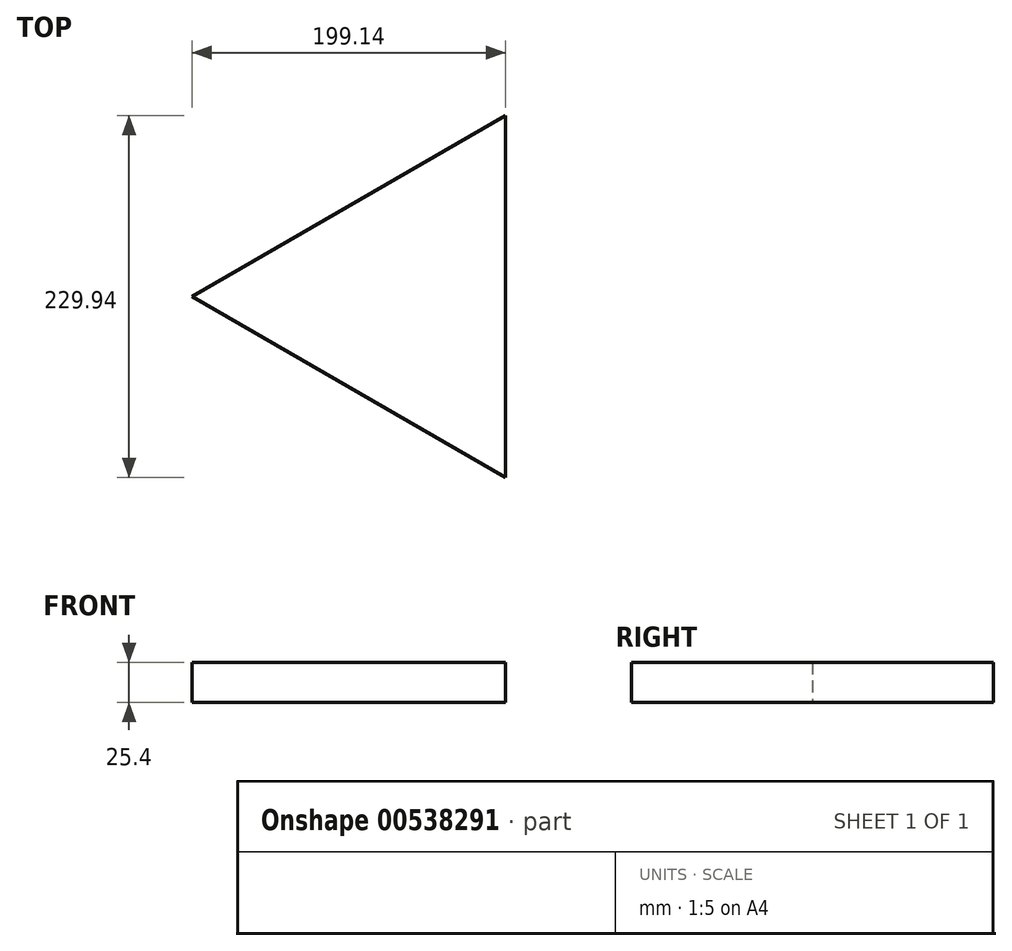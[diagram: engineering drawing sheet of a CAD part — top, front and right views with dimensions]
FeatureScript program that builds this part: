
annotation { "Feature Type Name" : "Feature", "Feature Type Description" : "" }
export const myFeature = defineFeature(function(context is Context, id is Id, definition is map)
    precondition{}
    {
        {
            var Q0;
            Q0=qCreatedBy(makeId("Top.planeOp"),FACE);
            var sketch = newSketch(context, id + "F0", { "sketchPlane" : qUnion([Q0])});
            skCircle(sketch, "E0.cCircle", {"center": v(-88.08, -142.62) * mm, "radius": 66.38 * mm, "construction": true});
            skLineSegment(sketch, "E0.0", {"start": v(-21.7, -27.65) * mm, "end": v(-21.7, -257.6) * mm});
            skLineSegment(sketch, "E0.1", {"start": v(-21.7, -257.6) * mm, "end": v(-220.84, -142.62) * mm});
            skLineSegment(sketch, "E0.2", {"start": v(-220.84, -142.62) * mm, "end": v(-21.7, -27.65) * mm});
            skPoint(sketch, "E0.0.midPoint", {"position": v(-21.7, -142.62) * mm});
            skSolve(sketch);
        }
        {
            var Q0;
            Q0 = qSketchRegion(id + "F0", true);
            extrude(context, id + "F1", {"entities" : qUnion([Q0]), "depth" : 25.4 * mm, "offsetDistance" : 25.4 * mm});
        }
    });
